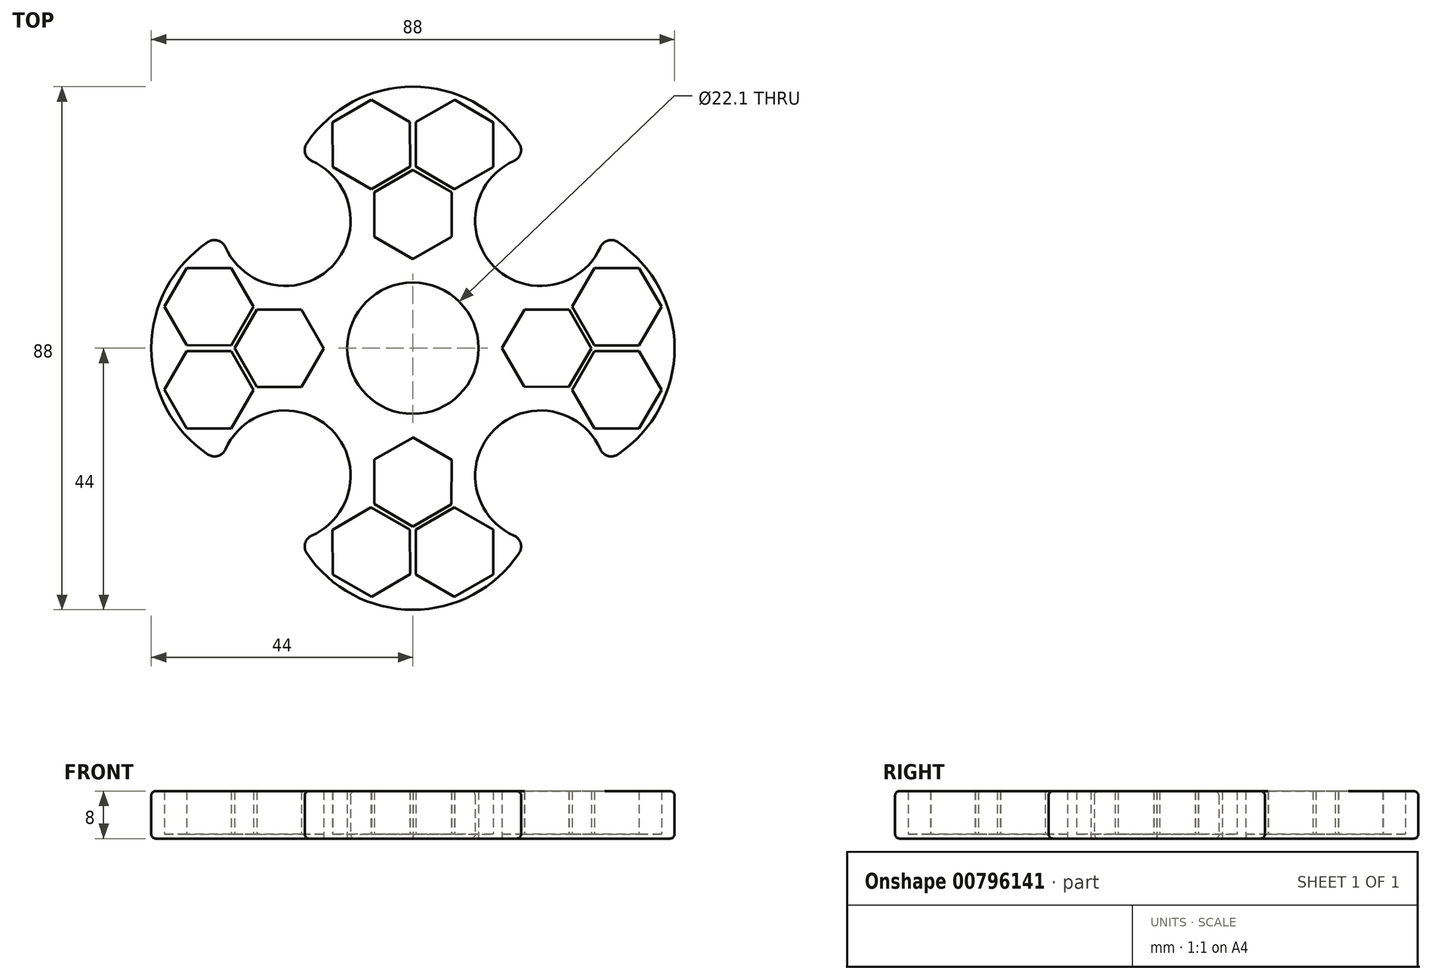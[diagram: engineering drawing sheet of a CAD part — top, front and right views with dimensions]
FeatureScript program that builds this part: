
annotation { "Feature Type Name" : "Feature", "Feature Type Description" : "" }
export const myFeature = defineFeature(function(context is Context, id is Id, definition is map)
    precondition{}
    {
        {
            var Q0;
            Q0=qCreatedBy(makeId("Top.planeOp"),FACE);
            var sketch = newSketch(context, id + "F0", { "sketchPlane" : qUnion([Q0])});
            skCircle(sketch, "E0", {"center": v(0, 0) * mm, "radius": 11.05 * mm});
            skCircle(sketch, "E1", {"center": v(0, 0) * mm, "radius": 35 * mm, "construction": true});
            skPoint(sketch, "E2", {"position": v(-35, 0) * mm});
            skPoint(sketch, "E3", {"position": v(35, 0) * mm});
            skPoint(sketch, "E4", {"position": v(0, 35) * mm});
            skPoint(sketch, "E5", {"position": v(0, -35) * mm});
            skPoint(sketch, "E6.0.midPoint", {"position": v(-28.5, 0) * mm});
            skPoint(sketch, "E7.0.midPoint", {"position": v(28.5, 0) * mm});
            skPoint(sketch, "E8.0.midPoint", {"position": v(0, 28.98) * mm});
            skPoint(sketch, "E9.0.midPoint", {"position": v(0, -28.02) * mm});
            skCircle(sketch, "E10", {"center": v(0, 0) * mm, "radius": 15 * mm});
            skLineSegment(sketch, "E11", {"start": v(0, 0) * mm, "end": v(-35, 0) * mm, "construction": true});
            skLineSegment(sketch, "E12", {"start": v(0, 0) * mm, "end": v(35, 0) * mm, "construction": true});
            skLineSegment(sketch, "E13", {"start": v(0, 0) * mm, "end": v(0, -35) * mm, "construction": true});
            skLineSegment(sketch, "E14", {"start": v(0, 0) * mm, "end": v(0, 35) * mm, "construction": true});
            skLineSegment(sketch, "E15.0", {"start": v(0, 5) * mm, "end": v(-30.51, 5) * mm});
            skLineSegment(sketch, "E16.0", {"start": v(0, -5) * mm, "end": v(30.51, -5) * mm});
            skLineSegment(sketch, "E17.0", {"start": v(0, 5) * mm, "end": v(30.51, 5) * mm});
            skLineSegment(sketch, "E18.0", {"start": v(0, -5) * mm, "end": v(-30.51, -5) * mm});
            skLineSegment(sketch, "E19.0", {"start": v(-5, 0.48) * mm, "end": v(-5, -30.03) * mm});
            skLineSegment(sketch, "E20.0", {"start": v(5, 0.48) * mm, "end": v(5, -30.03) * mm});
            skLineSegment(sketch, "E21.0", {"start": v(5, 0.48) * mm, "end": v(5, 30.98) * mm});
            skLineSegment(sketch, "E22.0", {"start": v(-5, 0.48) * mm, "end": v(-5, 30.98) * mm});
            skLineSegment(sketch, "E23", {"start": v(0, 0) * mm, "end": v(-24.75, 24.75) * mm, "construction": true});
            skLineSegment(sketch, "E24", {"start": v(24.75, -24.75) * mm, "end": v(0, 0) * mm, "construction": true});
            skLineSegment(sketch, "E25", {"start": v(24.75, 24.75) * mm, "end": v(0, 0) * mm, "construction": true});
            skLineSegment(sketch, "E26", {"start": v(-24.75, -24.75) * mm, "end": v(0, 0) * mm, "construction": true});
            skPoint(sketch, "E27", {"position": v(-7, 34.3) * mm});
            skPoint(sketch, "E28", {"position": v(7, 34.3) * mm});
            skPoint(sketch, "E29", {"position": v(-34.3, 7) * mm});
            skPoint(sketch, "E30", {"position": v(-34.3, -7) * mm});
            skPoint(sketch, "E31", {"position": v(34.3, 7) * mm});
            skPoint(sketch, "E32", {"position": v(34.3, -7) * mm});
            skPoint(sketch, "E33", {"position": v(7, -34.3) * mm});
            skPoint(sketch, "E34", {"position": v(-7, -34.3) * mm});
            skCircle(sketch, "E35.cCircle", {"center": v(-7, -34.3) * mm, "radius": 6.5 * mm, "construction": true});
            skLineSegment(sketch, "E35.0", {"start": v(-0.52, -30.5) * mm, "end": v(-0.48, -38.01) * mm});
            skLineSegment(sketch, "E35.1", {"start": v(-0.48, -38.01) * mm, "end": v(-6.96, -41.8) * mm});
            skLineSegment(sketch, "E35.2", {"start": v(-6.96, -41.8) * mm, "end": v(-13.48, -38.08) * mm});
            skLineSegment(sketch, "E35.3", {"start": v(-13.48, -38.08) * mm, "end": v(-13.52, -30.57) * mm});
            skLineSegment(sketch, "E35.4", {"start": v(-13.52, -30.57) * mm, "end": v(-7.04, -26.79) * mm});
            skLineSegment(sketch, "E35.5", {"start": v(-7.04, -26.79) * mm, "end": v(-0.52, -30.5) * mm});
            skPoint(sketch, "E35.0.midPoint", {"position": v(-0.5, -34.26) * mm});
            skPoint(sketch, "E36.0.midPoint", {"position": v(0.5, -30.6) * mm});
            skCircle(sketch, "E37.cCircle", {"center": v(34.3, -7) * mm, "radius": 6.5 * mm, "construction": true});
            skLineSegment(sketch, "E37.0", {"start": v(30.54, -0.5) * mm, "end": v(38.05, -0.5) * mm});
            skLineSegment(sketch, "E37.1", {"start": v(38.05, -0.5) * mm, "end": v(41.8, -7) * mm});
            skLineSegment(sketch, "E37.2", {"start": v(41.8, -7) * mm, "end": v(38.05, -13.5) * mm});
            skLineSegment(sketch, "E37.3", {"start": v(38.05, -13.5) * mm, "end": v(30.54, -13.5) * mm});
            skLineSegment(sketch, "E37.4", {"start": v(30.54, -13.5) * mm, "end": v(26.79, -7) * mm});
            skLineSegment(sketch, "E37.5", {"start": v(26.79, -7) * mm, "end": v(30.54, -0.5) * mm});
            skPoint(sketch, "E37.0.midPoint", {"position": v(34.3, -0.5) * mm});
            skCircle(sketch, "E38.cCircle", {"center": v(34.3, 7) * mm, "radius": 6.5 * mm, "construction": true});
            skLineSegment(sketch, "E38.0", {"start": v(38.05, 0.5) * mm, "end": v(30.54, 0.5) * mm});
            skLineSegment(sketch, "E38.1", {"start": v(30.54, 0.5) * mm, "end": v(26.79, 7) * mm});
            skLineSegment(sketch, "E38.2", {"start": v(26.79, 7) * mm, "end": v(30.54, 13.5) * mm});
            skLineSegment(sketch, "E38.3", {"start": v(30.54, 13.5) * mm, "end": v(38.04, 13.5) * mm});
            skLineSegment(sketch, "E38.4", {"start": v(38.04, 13.5) * mm, "end": v(41.8, 7) * mm});
            skLineSegment(sketch, "E38.5", {"start": v(41.8, 7) * mm, "end": v(38.05, 0.5) * mm});
            skPoint(sketch, "E38.0.midPoint", {"position": v(34.3, 0.5) * mm});
            skCircle(sketch, "E39.cCircle", {"center": v(7, 34.3) * mm, "radius": 6.5 * mm, "construction": true});
            skLineSegment(sketch, "E39.0", {"start": v(0.49, 30.56) * mm, "end": v(0.51, 38.06) * mm});
            skLineSegment(sketch, "E39.1", {"start": v(0.51, 38.06) * mm, "end": v(7.02, 41.8) * mm});
            skLineSegment(sketch, "E39.2", {"start": v(7.02, 41.8) * mm, "end": v(13.51, 38.03) * mm});
            skLineSegment(sketch, "E39.3", {"start": v(13.51, 38.03) * mm, "end": v(13.49, 30.52) * mm});
            skLineSegment(sketch, "E39.4", {"start": v(13.49, 30.52) * mm, "end": v(6.98, 26.79) * mm});
            skLineSegment(sketch, "E39.5", {"start": v(6.98, 26.79) * mm, "end": v(0.49, 30.56) * mm});
            skPoint(sketch, "E39.0.midPoint", {"position": v(0.5, 34.31) * mm});
            skCircle(sketch, "E40.cCircle", {"center": v(-7, 34.3) * mm, "radius": 6.5 * mm, "construction": true});
            skLineSegment(sketch, "E40.0", {"start": v(-0.51, 38.07) * mm, "end": v(-0.49, 30.56) * mm});
            skLineSegment(sketch, "E40.1", {"start": v(-0.49, 30.56) * mm, "end": v(-6.97, 26.79) * mm});
            skLineSegment(sketch, "E40.2", {"start": v(-6.97, 26.79) * mm, "end": v(-13.49, 30.52) * mm});
            skLineSegment(sketch, "E40.3", {"start": v(-13.49, 30.52) * mm, "end": v(-13.51, 38.02) * mm});
            skLineSegment(sketch, "E40.4", {"start": v(-13.51, 38.02) * mm, "end": v(-7.03, 41.8) * mm});
            skLineSegment(sketch, "E40.5", {"start": v(-7.03, 41.8) * mm, "end": v(-0.51, 38.07) * mm});
            skPoint(sketch, "E40.0.midPoint", {"position": v(-0.5, 34.32) * mm});
            skCircle(sketch, "E41.cCircle", {"center": v(-34.3, 7) * mm, "radius": 6.5 * mm, "construction": true});
            skLineSegment(sketch, "E41.0", {"start": v(-30.55, 0.5) * mm, "end": v(-38.05, 0.5) * mm});
            skLineSegment(sketch, "E41.1", {"start": v(-38.05, 0.5) * mm, "end": v(-41.8, 7) * mm});
            skLineSegment(sketch, "E41.2", {"start": v(-41.8, 7) * mm, "end": v(-38.04, 13.5) * mm});
            skLineSegment(sketch, "E41.3", {"start": v(-38.04, 13.5) * mm, "end": v(-30.53, 13.5) * mm});
            skLineSegment(sketch, "E41.4", {"start": v(-30.53, 13.5) * mm, "end": v(-26.79, 7) * mm});
            skLineSegment(sketch, "E41.5", {"start": v(-26.79, 7) * mm, "end": v(-30.55, 0.5) * mm});
            skPoint(sketch, "E41.0.midPoint", {"position": v(-34.3, 0.5) * mm});
            skCircle(sketch, "E42.cCircle", {"center": v(-34.3, -7) * mm, "radius": 6.5 * mm, "construction": true});
            skLineSegment(sketch, "E42.0", {"start": v(-38.03, -0.5) * mm, "end": v(-30.53, -0.5) * mm});
            skLineSegment(sketch, "E42.1", {"start": v(-30.53, -0.5) * mm, "end": v(-26.79, -7.01) * mm});
            skLineSegment(sketch, "E42.2", {"start": v(-26.79, -7.01) * mm, "end": v(-30.55, -13.5) * mm});
            skLineSegment(sketch, "E42.3", {"start": v(-30.55, -13.5) * mm, "end": v(-38.06, -13.5) * mm});
            skLineSegment(sketch, "E42.4", {"start": v(-38.06, -13.5) * mm, "end": v(-41.8, -6.99) * mm});
            skLineSegment(sketch, "E42.5", {"start": v(-41.8, -6.99) * mm, "end": v(-38.03, -0.5) * mm});
            skPoint(sketch, "E42.0.midPoint", {"position": v(-34.28, -0.5) * mm});
            skCircle(sketch, "E43", {"center": v(0, 0) * mm, "radius": 22.5 * mm, "construction": true});
            skPoint(sketch, "E44", {"position": v(-22.5, 0) * mm});
            skPoint(sketch, "E45", {"position": v(0, 22.5) * mm});
            skPoint(sketch, "E46", {"position": v(22.5, 0) * mm});
            skPoint(sketch, "E47", {"position": v(0, -22.5) * mm});
            skCircle(sketch, "E48.cCircle", {"center": v(7, -34.3) * mm, "radius": 6.5 * mm, "construction": true});
            skLineSegment(sketch, "E48.0", {"start": v(0.5, -38.05) * mm, "end": v(0.5, -30.54) * mm});
            skLineSegment(sketch, "E48.1", {"start": v(0.5, -30.54) * mm, "end": v(7, -26.79) * mm});
            skLineSegment(sketch, "E48.2", {"start": v(7, -26.79) * mm, "end": v(13.5, -30.54) * mm});
            skLineSegment(sketch, "E48.3", {"start": v(13.5, -30.54) * mm, "end": v(13.5, -38.05) * mm});
            skLineSegment(sketch, "E48.4", {"start": v(13.5, -38.05) * mm, "end": v(7, -41.8) * mm});
            skLineSegment(sketch, "E48.5", {"start": v(7, -41.8) * mm, "end": v(0.5, -38.05) * mm});
            skPoint(sketch, "E48.0.midPoint", {"position": v(0.5, -34.3) * mm});
            skCircle(sketch, "E49.cCircle", {"center": v(0, 22.5) * mm, "radius": 6.5 * mm, "construction": true});
            skLineSegment(sketch, "E49.0", {"start": v(0, 15) * mm, "end": v(-6.5, 18.74) * mm});
            skLineSegment(sketch, "E49.1", {"start": v(-6.5, 18.74) * mm, "end": v(-6.5, 26.25) * mm});
            skLineSegment(sketch, "E49.2", {"start": v(-6.5, 26.25) * mm, "end": v(0, 30) * mm});
            skLineSegment(sketch, "E49.3", {"start": v(0, 30) * mm, "end": v(6.5, 26.26) * mm});
            skLineSegment(sketch, "E49.4", {"start": v(6.5, 26.26) * mm, "end": v(6.5, 18.75) * mm});
            skLineSegment(sketch, "E49.5", {"start": v(6.5, 18.75) * mm, "end": v(0, 15) * mm});
            skPoint(sketch, "E49.0.midPoint", {"position": v(-3.24, 16.87) * mm});
            skCircle(sketch, "E50.cCircle", {"center": v(-22.5, 0) * mm, "radius": 6.5 * mm, "construction": true});
            skLineSegment(sketch, "E50.0", {"start": v(-15, -0.02) * mm, "end": v(-18.76, -6.5) * mm});
            skLineSegment(sketch, "E50.1", {"start": v(-18.76, -6.5) * mm, "end": v(-26.27, -6.5) * mm});
            skLineSegment(sketch, "E50.2", {"start": v(-26.27, -6.5) * mm, "end": v(-30, 0.02) * mm});
            skLineSegment(sketch, "E50.3", {"start": v(-30, 0.02) * mm, "end": v(-26.24, 6.5) * mm});
            skLineSegment(sketch, "E50.4", {"start": v(-26.24, 6.5) * mm, "end": v(-18.73, 6.5) * mm});
            skLineSegment(sketch, "E50.5", {"start": v(-18.73, 6.5) * mm, "end": v(-15, -0.02) * mm});
            skPoint(sketch, "E50.0.midPoint", {"position": v(-16.88, -3.26) * mm});
            skCircle(sketch, "E51.cCircle", {"center": v(0, -22.5) * mm, "radius": 6.5 * mm, "construction": true});
            skLineSegment(sketch, "E51.0", {"start": v(-0.03, -30) * mm, "end": v(-6.51, -26.23) * mm});
            skLineSegment(sketch, "E51.1", {"start": v(-6.51, -26.23) * mm, "end": v(-6.49, -18.72) * mm});
            skLineSegment(sketch, "E51.2", {"start": v(-6.49, -18.72) * mm, "end": v(0.03, -15) * mm});
            skLineSegment(sketch, "E51.3", {"start": v(0.03, -15) * mm, "end": v(6.51, -18.77) * mm});
            skLineSegment(sketch, "E51.4", {"start": v(6.51, -18.77) * mm, "end": v(6.49, -26.28) * mm});
            skLineSegment(sketch, "E51.5", {"start": v(6.49, -26.28) * mm, "end": v(-0.03, -30) * mm});
            skPoint(sketch, "E51.0.midPoint", {"position": v(-3.27, -28.12) * mm});
            skCircle(sketch, "E52.cCircle", {"center": v(22.5, 0) * mm, "radius": 6.5 * mm, "construction": true});
            skLineSegment(sketch, "E52.0", {"start": v(30, -0.04) * mm, "end": v(26.22, -6.52) * mm});
            skLineSegment(sketch, "E52.1", {"start": v(26.22, -6.52) * mm, "end": v(18.71, -6.48) * mm});
            skLineSegment(sketch, "E52.2", {"start": v(18.71, -6.48) * mm, "end": v(15, 0.04) * mm});
            skLineSegment(sketch, "E52.3", {"start": v(15, 0.04) * mm, "end": v(18.78, 6.52) * mm});
            skLineSegment(sketch, "E52.4", {"start": v(18.78, 6.52) * mm, "end": v(26.29, 6.48) * mm});
            skLineSegment(sketch, "E52.5", {"start": v(26.29, 6.48) * mm, "end": v(30, -0.04) * mm});
            skPoint(sketch, "E52.0.midPoint", {"position": v(28.11, -3.28) * mm});
            skCircle(sketch, "E53", {"center": v(22.5, 0) * mm, "radius": 21.5 * mm});
            skCircle(sketch, "E54", {"center": v(0, 22.5) * mm, "radius": 21.5 * mm});
            skCircle(sketch, "E55", {"center": v(-22.5, 0) * mm, "radius": 21.5 * mm});
            skCircle(sketch, "E56", {"center": v(0, -22.5) * mm, "radius": 21.5 * mm});
            skPoint(sketch, "E57", {"position": v(-21.48, -21.48) * mm});
            skPoint(sketch, "E58", {"position": v(21.48, -21.48) * mm});
            skPoint(sketch, "E59", {"position": v(21.48, 21.48) * mm});
            skPoint(sketch, "E60", {"position": v(-21.48, 21.48) * mm});
            skCircle(sketch, "E61", {"center": v(-21.48, -21.48) * mm, "radius": 11 * mm});
            skCircle(sketch, "E62", {"center": v(-21.48, 21.48) * mm, "radius": 11 * mm});
            skCircle(sketch, "E63", {"center": v(21.48, 21.48) * mm, "radius": 11 * mm});
            skCircle(sketch, "E64", {"center": v(21.48, -21.48) * mm, "radius": 11 * mm});
            skSolve(sketch);
        }
        {
            var Q0;
            {var subQ18=sQuery(id+"F0.wireOp",EDGE,"E41.0");Q0=makeQuery(id+"F0.imprint","IMPRINT",FACE,{"disambiguationData":[TD([[makeQuery(id+"F0.imprint","IMPRINT",EDGE,{"derivedFrom":subQ18}),1.0]])]});}
            var Q1;
            {var subQ23=sQuery(id+"F0.wireOp",EDGE,"E39.0");Q1=makeQuery(id+"F0.imprint","IMPRINT",FACE,{"disambiguationData":[TD([[makeQuery(id+"F0.imprint","IMPRINT",EDGE,{"derivedFrom":subQ23}),1.0]])]});}
            var Q2;
            {var subQ18=sQuery(id+"F0.wireOp",EDGE,"E37.0");Q2=makeQuery(id+"F0.imprint","IMPRINT",FACE,{"disambiguationData":[TD([[makeQuery(id+"F0.imprint","IMPRINT",EDGE,{"derivedFrom":subQ18}),1.0]])]});}
            var Q3;
            {var subQ18=sQuery(id+"F0.wireOp",EDGE,"E35.0");Q3=makeQuery(id+"F0.imprint","IMPRINT",FACE,{"disambiguationData":[TD([[makeQuery(id+"F0.imprint","IMPRINT",EDGE,{"derivedFrom":subQ18}),1.0]])]});}
            var Q4;
            {var subQ1=sQuery(id+"F0.wireOp",EDGE,"E0");var subQ8=sQuery(id+"F0.wireOp",EDGE,"E18.0");var subQ10=makeQuery(id+"F0.imprint","INTERSECT",VERTEX,{"derivedFrom":[subQ1,subQ8]});Q4=makeQuery(id+"F0.imprint","IMPRINT",FACE,{"disambiguationData":[TD([[makeQuery(id+"F0.imprint","IMPRINT",EDGE,{"disambiguationData":[TD([[subQ10,-1.0]])],"derivedFrom":subQ1}),-1.0]])]});}
            var Q5;
            {var subQ3=sQuery(id+"F0.wireOp",EDGE,"E54");var subQ9=sQuery(id+"F0.wireOp",EDGE,"E0");var subQ10=makeQuery(id+"F0.imprint","INTERSECT",VERTEX,{"disambiguationData":[OD(1.0)],"derivedFrom":[subQ9,subQ3]});Q5=makeQuery(id+"F0.imprint","IMPRINT",FACE,{"disambiguationData":[TD([[makeQuery(id+"F0.imprint","IMPRINT",EDGE,{"disambiguationData":[TD([[subQ10,-1.0]])],"derivedFrom":subQ9}),-1.0]])]});}
            var Q6;
            {var subQ0=sQuery(id+"F0.wireOp",EDGE,"E22.0");var subQ1=sQuery(id+"F0.wireOp",EDGE,"E0");var subQ2=makeQuery(id+"F0.imprint","INTERSECT",VERTEX,{"derivedFrom":[subQ1,subQ0]});Q6=makeQuery(id+"F0.imprint","IMPRINT",FACE,{"disambiguationData":[TD([[makeQuery(id+"F0.imprint","IMPRINT",EDGE,{"disambiguationData":[TD([[subQ2,-1.0]])],"derivedFrom":subQ1}),-1.0]])]});}
            var Q7;
            {var subQ3=sQuery(id+"F0.wireOp",EDGE,"E53");var subQ11=sQuery(id+"F0.wireOp",EDGE,"E0");var subQ16=makeQuery(id+"F0.imprint","INTERSECT",VERTEX,{"disambiguationData":[OD(0.0)],"derivedFrom":[subQ11,subQ3]});Q7=makeQuery(id+"F0.imprint","IMPRINT",FACE,{"disambiguationData":[TD([[makeQuery(id+"F0.imprint","IMPRINT",EDGE,{"disambiguationData":[TD([[subQ16,-1.0]])],"derivedFrom":subQ11}),-1.0]])]});}
            var Q8;
            {var subQ0=sQuery(id+"F0.wireOp",EDGE,"E17.0");var subQ1=sQuery(id+"F0.wireOp",EDGE,"E0");var subQ2=makeQuery(id+"F0.imprint","INTERSECT",VERTEX,{"derivedFrom":[subQ1,subQ0]});Q8=makeQuery(id+"F0.imprint","IMPRINT",FACE,{"disambiguationData":[TD([[makeQuery(id+"F0.imprint","IMPRINT",EDGE,{"disambiguationData":[TD([[subQ2,-1.0]])],"derivedFrom":subQ1}),-1.0]])]});}
            var Q9;
            {var subQ5=sQuery(id+"F0.wireOp",EDGE,"E0");var subQ13=sQuery(id+"F0.wireOp",EDGE,"E54");var subQ14=makeQuery(id+"F0.imprint","INTERSECT",VERTEX,{"disambiguationData":[OD(0.0)],"derivedFrom":[subQ5,subQ13]});Q9=makeQuery(id+"F0.imprint","IMPRINT",FACE,{"disambiguationData":[TD([[makeQuery(id+"F0.imprint","IMPRINT",EDGE,{"disambiguationData":[TD([[subQ14,1.0]])],"derivedFrom":subQ5}),-1.0]])]});}
            var Q10;
            {var subQ0=sQuery(id+"F0.wireOp",EDGE,"E20.0");var subQ1=sQuery(id+"F0.wireOp",EDGE,"E0");var subQ2=makeQuery(id+"F0.imprint","INTERSECT",VERTEX,{"derivedFrom":[subQ1,subQ0]});Q10=makeQuery(id+"F0.imprint","IMPRINT",FACE,{"disambiguationData":[TD([[makeQuery(id+"F0.imprint","IMPRINT",EDGE,{"disambiguationData":[TD([[subQ2,-1.0]])],"derivedFrom":subQ1}),-1.0]])]});}
            var Q11;
            {var subQ7=sQuery(id+"F0.wireOp",EDGE,"E55");var subQ12=sQuery(id+"F0.wireOp",EDGE,"E0");var subQ13=makeQuery(id+"F0.imprint","INTERSECT",VERTEX,{"disambiguationData":[OD(1.0)],"derivedFrom":[subQ12,subQ7]});Q11=makeQuery(id+"F0.imprint","IMPRINT",FACE,{"disambiguationData":[TD([[makeQuery(id+"F0.imprint","IMPRINT",EDGE,{"disambiguationData":[TD([[subQ13,-1.0]])],"derivedFrom":subQ12}),-1.0]])]});}
            var Q12;
            {var subQ0=sQuery(id+"F0.wireOp",EDGE,"E56");var subQ1=sQuery(id+"F0.wireOp",EDGE,"E10");var subQ2=makeQuery(id+"F0.imprint","INTERSECT",VERTEX,{"disambiguationData":[OD(0.0)],"derivedFrom":[subQ1,subQ0]});Q12=makeQuery(id+"F0.imprint","IMPRINT",FACE,{"disambiguationData":[TD([[makeQuery(id+"F0.imprint","IMPRINT",EDGE,{"disambiguationData":[TD([[subQ2,-1.0]])],"derivedFrom":subQ1}),-1.0]])]});}
            var Q13;
            {var subQ0=sQuery(id+"F0.wireOp",EDGE,"E55");var subQ1=sQuery(id+"F0.wireOp",EDGE,"E10");var subQ2=makeQuery(id+"F0.imprint","INTERSECT",VERTEX,{"disambiguationData":[OD(0.0)],"derivedFrom":[subQ1,subQ0]});Q13=makeQuery(id+"F0.imprint","IMPRINT",FACE,{"disambiguationData":[TD([[makeQuery(id+"F0.imprint","IMPRINT",EDGE,{"disambiguationData":[TD([[subQ2,-1.0]])],"derivedFrom":subQ1}),-1.0]])]});}
            var Q14;
            {var subQ0=sQuery(id+"F0.wireOp",EDGE,"E54");var subQ1=sQuery(id+"F0.wireOp",EDGE,"E10");var subQ2=makeQuery(id+"F0.imprint","INTERSECT",VERTEX,{"disambiguationData":[OD(0.0)],"derivedFrom":[subQ1,subQ0]});Q14=makeQuery(id+"F0.imprint","IMPRINT",FACE,{"disambiguationData":[TD([[makeQuery(id+"F0.imprint","IMPRINT",EDGE,{"disambiguationData":[TD([[subQ2,-1.0]])],"derivedFrom":subQ1}),-1.0]])]});}
            var Q15;
            {var subQ0=sQuery(id+"F0.wireOp",EDGE,"E53");var subQ1=sQuery(id+"F0.wireOp",EDGE,"E10");var subQ2=makeQuery(id+"F0.imprint","INTERSECT",VERTEX,{"disambiguationData":[OD(1.0)],"derivedFrom":[subQ1,subQ0]});Q15=makeQuery(id+"F0.imprint","IMPRINT",FACE,{"disambiguationData":[TD([[makeQuery(id+"F0.imprint","IMPRINT",EDGE,{"disambiguationData":[TD([[subQ2,-1.0]])],"derivedFrom":subQ1}),-1.0]])]});}
            var Q16;
            {var subQ0=sQuery(id+"F0.wireOp",EDGE,"E50.0");var subQ1=sQuery(id+"F0.wireOp",EDGE,"E10");var subQ2=makeQuery(id+"F0.imprint","INTERSECT",VERTEX,{"derivedFrom":[subQ1,subQ0]});Q16=makeQuery(id+"F0.imprint","IMPRINT",FACE,{"disambiguationData":[TD([[makeQuery(id+"F0.imprint","IMPRINT",EDGE,{"disambiguationData":[TD([[subQ2,-1.0]])],"derivedFrom":subQ1}),-1.0]])]});}
            var Q17;
            {var subQ0=sQuery(id+"F0.wireOp",EDGE,"E15.0");var subQ1=sQuery(id+"F0.wireOp",EDGE,"E10");var subQ2=makeQuery(id+"F0.imprint","INTERSECT",VERTEX,{"derivedFrom":[subQ1,subQ0]});Q17=makeQuery(id+"F0.imprint","IMPRINT",FACE,{"disambiguationData":[TD([[makeQuery(id+"F0.imprint","IMPRINT",EDGE,{"disambiguationData":[TD([[subQ2,-1.0]])],"derivedFrom":subQ1}),-1.0]])]});}
            var Q18;
            {var subQ0=sQuery(id+"F0.wireOp",EDGE,"E49.0");var subQ1=sQuery(id+"F0.wireOp",EDGE,"E10");var subQ2=makeQuery(id+"F0.imprint","INTERSECT",VERTEX,{"derivedFrom":[subQ1,subQ0]});Q18=makeQuery(id+"F0.imprint","IMPRINT",FACE,{"disambiguationData":[TD([[makeQuery(id+"F0.imprint","IMPRINT",EDGE,{"disambiguationData":[TD([[subQ2,-1.0]])],"derivedFrom":subQ1}),-1.0]])]});}
            var Q19;
            {var subQ0=sQuery(id+"F0.wireOp",EDGE,"E21.0");var subQ1=sQuery(id+"F0.wireOp",EDGE,"E10");var subQ2=makeQuery(id+"F0.imprint","INTERSECT",VERTEX,{"derivedFrom":[subQ1,subQ0]});Q19=makeQuery(id+"F0.imprint","IMPRINT",FACE,{"disambiguationData":[TD([[makeQuery(id+"F0.imprint","IMPRINT",EDGE,{"disambiguationData":[TD([[subQ2,-1.0]])],"derivedFrom":subQ1}),-1.0]])]});}
            var Q20;
            {var subQ0=sQuery(id+"F0.wireOp",EDGE,"E52.3");var subQ1=sQuery(id+"F0.wireOp",EDGE,"E10");var subQ2=makeQuery(id+"F0.imprint","INTERSECT",VERTEX,{"derivedFrom":[subQ1,subQ0]});Q20=makeQuery(id+"F0.imprint","IMPRINT",FACE,{"disambiguationData":[TD([[makeQuery(id+"F0.imprint","IMPRINT",EDGE,{"disambiguationData":[TD([[subQ2,-1.0]])],"derivedFrom":subQ1}),-1.0]])]});}
            var Q21;
            {var subQ0=sQuery(id+"F0.wireOp",EDGE,"E52.2");var subQ1=sQuery(id+"F0.wireOp",EDGE,"E10");var subQ2=makeQuery(id+"F0.imprint","INTERSECT",VERTEX,{"derivedFrom":[subQ1,subQ0]});Q21=makeQuery(id+"F0.imprint","IMPRINT",FACE,{"disambiguationData":[TD([[makeQuery(id+"F0.imprint","IMPRINT",EDGE,{"disambiguationData":[TD([[subQ2,1.0]])],"derivedFrom":subQ1}),-1.0]])]});}
            var Q22;
            {var subQ0=sQuery(id+"F0.wireOp",EDGE,"E51.3");var subQ1=sQuery(id+"F0.wireOp",EDGE,"E10");var subQ2=makeQuery(id+"F0.imprint","INTERSECT",VERTEX,{"derivedFrom":[subQ1,subQ0]});Q22=makeQuery(id+"F0.imprint","IMPRINT",FACE,{"disambiguationData":[TD([[makeQuery(id+"F0.imprint","IMPRINT",EDGE,{"disambiguationData":[TD([[subQ2,-1.0]])],"derivedFrom":subQ1}),-1.0]])]});}
            var Q23;
            {var subQ0=sQuery(id+"F0.wireOp",EDGE,"E19.0");var subQ1=sQuery(id+"F0.wireOp",EDGE,"E10");var subQ2=makeQuery(id+"F0.imprint","INTERSECT",VERTEX,{"derivedFrom":[subQ1,subQ0]});Q23=makeQuery(id+"F0.imprint","IMPRINT",FACE,{"disambiguationData":[TD([[makeQuery(id+"F0.imprint","IMPRINT",EDGE,{"disambiguationData":[TD([[subQ2,-1.0]])],"derivedFrom":subQ1}),-1.0]])]});}
            var Q24;
            {var subQ0=sQuery(id+"F0.wireOp",EDGE,"E22.0");var subQ1=sQuery(id+"F0.wireOp",EDGE,"E10");var subQ2=makeQuery(id+"F0.imprint","INTERSECT",VERTEX,{"derivedFrom":[subQ1,subQ0]});Q24=makeQuery(id+"F0.imprint","IMPRINT",FACE,{"disambiguationData":[TD([[makeQuery(id+"F0.imprint","IMPRINT",EDGE,{"disambiguationData":[TD([[subQ2,-1.0]])],"derivedFrom":subQ1}),1.0]])]});}
            var Q25;
            {var subQ0=sQuery(id+"F0.wireOp",EDGE,"E55");var subQ1=sQuery(id+"F0.wireOp",EDGE,"E0");var subQ2=makeQuery(id+"F0.imprint","INTERSECT",VERTEX,{"disambiguationData":[OD(0.0)],"derivedFrom":[subQ1,subQ0]});Q25=makeQuery(id+"F0.imprint","IMPRINT",FACE,{"disambiguationData":[TD([[makeQuery(id+"F0.imprint","IMPRINT",EDGE,{"disambiguationData":[TD([[subQ2,-1.0]])],"derivedFrom":subQ1}),-1.0]])]});}
            var Q26;
            {var subQ0=sQuery(id+"F0.wireOp",EDGE,"E21.0");var subQ1=sQuery(id+"F0.wireOp",EDGE,"E0");var subQ2=makeQuery(id+"F0.imprint","INTERSECT",VERTEX,{"derivedFrom":[subQ1,subQ0]});Q26=makeQuery(id+"F0.imprint","IMPRINT",FACE,{"disambiguationData":[TD([[makeQuery(id+"F0.imprint","IMPRINT",EDGE,{"disambiguationData":[TD([[subQ2,-1.0]])],"derivedFrom":subQ1}),-1.0]])]});}
            var Q27;
            {var subQ0=sQuery(id+"F0.wireOp",EDGE,"E17.0");var subQ1=sQuery(id+"F0.wireOp",EDGE,"E10");var subQ2=makeQuery(id+"F0.imprint","INTERSECT",VERTEX,{"derivedFrom":[subQ1,subQ0]});Q27=makeQuery(id+"F0.imprint","IMPRINT",FACE,{"disambiguationData":[TD([[makeQuery(id+"F0.imprint","IMPRINT",EDGE,{"disambiguationData":[TD([[subQ2,-1.0]])],"derivedFrom":subQ1}),1.0]])]});}
            var Q28;
            {var subQ0=sQuery(id+"F0.wireOp",EDGE,"E53");var subQ1=sQuery(id+"F0.wireOp",EDGE,"E10");var subQ2=makeQuery(id+"F0.imprint","INTERSECT",VERTEX,{"disambiguationData":[OD(0.0)],"derivedFrom":[subQ1,subQ0]});Q28=makeQuery(id+"F0.imprint","IMPRINT",FACE,{"disambiguationData":[TD([[makeQuery(id+"F0.imprint","IMPRINT",EDGE,{"disambiguationData":[TD([[subQ2,-1.0]])],"derivedFrom":subQ1}),1.0]])]});}
            var Q29;
            {var subQ0=sQuery(id+"F0.wireOp",EDGE,"E17.0");var subQ1=sQuery(id+"F0.wireOp",EDGE,"E0");var subQ2=makeQuery(id+"F0.imprint","INTERSECT",VERTEX,{"derivedFrom":[subQ1,subQ0]});Q29=makeQuery(id+"F0.imprint","IMPRINT",FACE,{"disambiguationData":[TD([[makeQuery(id+"F0.imprint","IMPRINT",EDGE,{"disambiguationData":[TD([[subQ2,1.0]])],"derivedFrom":subQ1}),-1.0]])]});}
            var Q30;
            {var subQ0=sQuery(id+"F0.wireOp",EDGE,"E56");var subQ1=sQuery(id+"F0.wireOp",EDGE,"E10");var subQ2=makeQuery(id+"F0.imprint","INTERSECT",VERTEX,{"disambiguationData":[OD(1.0)],"derivedFrom":[subQ1,subQ0]});Q30=makeQuery(id+"F0.imprint","IMPRINT",FACE,{"disambiguationData":[TD([[makeQuery(id+"F0.imprint","IMPRINT",EDGE,{"disambiguationData":[TD([[subQ2,-1.0]])],"derivedFrom":subQ1}),1.0]])]});}
            var Q31;
            {var subQ0=sQuery(id+"F0.wireOp",EDGE,"E16.0");var subQ1=sQuery(id+"F0.wireOp",EDGE,"E0");var subQ2=makeQuery(id+"F0.imprint","INTERSECT",VERTEX,{"derivedFrom":[subQ1,subQ0]});Q31=makeQuery(id+"F0.imprint","IMPRINT",FACE,{"disambiguationData":[TD([[makeQuery(id+"F0.imprint","IMPRINT",EDGE,{"disambiguationData":[TD([[subQ2,-1.0]])],"derivedFrom":subQ1}),-1.0]])]});}
            var Q32;
            {var subQ0=sQuery(id+"F0.wireOp",EDGE,"E20.0");var subQ1=sQuery(id+"F0.wireOp",EDGE,"E10");var subQ2=makeQuery(id+"F0.imprint","INTERSECT",VERTEX,{"derivedFrom":[subQ1,subQ0]});Q32=makeQuery(id+"F0.imprint","IMPRINT",FACE,{"disambiguationData":[TD([[makeQuery(id+"F0.imprint","IMPRINT",EDGE,{"disambiguationData":[TD([[subQ2,-1.0]])],"derivedFrom":subQ1}),1.0]])]});}
            var Q33;
            {var subQ0=sQuery(id+"F0.wireOp",EDGE,"E53");var subQ1=sQuery(id+"F0.wireOp",EDGE,"E0");var subQ2=makeQuery(id+"F0.imprint","INTERSECT",VERTEX,{"disambiguationData":[OD(1.0)],"derivedFrom":[subQ1,subQ0]});Q33=makeQuery(id+"F0.imprint","IMPRINT",FACE,{"disambiguationData":[TD([[makeQuery(id+"F0.imprint","IMPRINT",EDGE,{"disambiguationData":[TD([[subQ2,-1.0]])],"derivedFrom":subQ1}),-1.0]])]});}
            var Q34;
            {var subQ0=sQuery(id+"F0.wireOp",EDGE,"E19.0");var subQ1=sQuery(id+"F0.wireOp",EDGE,"E0");var subQ2=makeQuery(id+"F0.imprint","INTERSECT",VERTEX,{"derivedFrom":[subQ1,subQ0]});Q34=makeQuery(id+"F0.imprint","IMPRINT",FACE,{"disambiguationData":[TD([[makeQuery(id+"F0.imprint","IMPRINT",EDGE,{"disambiguationData":[TD([[subQ2,-1.0]])],"derivedFrom":subQ1}),-1.0]])]});}
            var Q35;
            {var subQ0=sQuery(id+"F0.wireOp",EDGE,"E55");var subQ1=sQuery(id+"F0.wireOp",EDGE,"E10");var subQ2=makeQuery(id+"F0.imprint","INTERSECT",VERTEX,{"disambiguationData":[OD(1.0)],"derivedFrom":[subQ1,subQ0]});Q35=makeQuery(id+"F0.imprint","IMPRINT",FACE,{"disambiguationData":[TD([[makeQuery(id+"F0.imprint","IMPRINT",EDGE,{"disambiguationData":[TD([[subQ2,-1.0]])],"derivedFrom":subQ1}),1.0]])]});}
            var Q36;
            {var subQ0=sQuery(id+"F0.wireOp",EDGE,"E56");var subQ1=sQuery(id+"F0.wireOp",EDGE,"E0");var subQ2=makeQuery(id+"F0.imprint","INTERSECT",VERTEX,{"disambiguationData":[OD(0.0)],"derivedFrom":[subQ1,subQ0]});Q36=makeQuery(id+"F0.imprint","IMPRINT",FACE,{"disambiguationData":[TD([[makeQuery(id+"F0.imprint","IMPRINT",EDGE,{"disambiguationData":[TD([[subQ2,-1.0]])],"derivedFrom":subQ1}),-1.0]])]});}
            var Q37;
            {var subQ0=sQuery(id+"F0.wireOp",EDGE,"E18.0");var subQ1=sQuery(id+"F0.wireOp",EDGE,"E10");var subQ2=makeQuery(id+"F0.imprint","INTERSECT",VERTEX,{"derivedFrom":[subQ1,subQ0]});Q37=makeQuery(id+"F0.imprint","IMPRINT",FACE,{"disambiguationData":[TD([[makeQuery(id+"F0.imprint","IMPRINT",EDGE,{"disambiguationData":[TD([[subQ2,-1.0]])],"derivedFrom":subQ1}),1.0]])]});}
            var Q38;
            {var subQ0=sQuery(id+"F0.wireOp",EDGE,"E15.0");var subQ1=sQuery(id+"F0.wireOp",EDGE,"E0");var subQ2=makeQuery(id+"F0.imprint","INTERSECT",VERTEX,{"derivedFrom":[subQ1,subQ0]});Q38=makeQuery(id+"F0.imprint","IMPRINT",FACE,{"disambiguationData":[TD([[makeQuery(id+"F0.imprint","IMPRINT",EDGE,{"disambiguationData":[TD([[subQ2,-1.0]])],"derivedFrom":subQ1}),-1.0]])]});}
            var Q39;
            {var subQ0=sQuery(id+"F0.wireOp",EDGE,"E54");var subQ1=sQuery(id+"F0.wireOp",EDGE,"E10");var subQ2=makeQuery(id+"F0.imprint","INTERSECT",VERTEX,{"disambiguationData":[OD(1.0)],"derivedFrom":[subQ1,subQ0]});Q39=makeQuery(id+"F0.imprint","IMPRINT",FACE,{"disambiguationData":[TD([[makeQuery(id+"F0.imprint","IMPRINT",EDGE,{"disambiguationData":[TD([[subQ2,-1.0]])],"derivedFrom":subQ1}),1.0]])]});}
            extrude(context, id + "F1", {"entities" : qUnion([Q0, Q1, Q2, Q3, Q4, Q5, Q6, Q7, Q8, Q9, Q10, Q11, Q12, Q13, Q14, Q15, Q16, Q17, Q18, Q19, Q20, Q21, Q22, Q23, Q24, Q25, Q26, Q27, Q28, Q29, Q30, Q31, Q32, Q33, Q34, Q35, Q36, Q37, Q38, Q39]), "depth" : 8 * mm, "offsetDistance" : 25 * mm});
        }
        {
            var Q0;
            {var subQ1=sQuery(id+"F0.wireOp",EDGE,"E10");var subQ8=sQuery(id+"F0.wireOp",EDGE,"E50.5");var subQ13=makeQuery(id+"F0.imprint","INTERSECT",VERTEX,{"derivedFrom":[subQ1,subQ8]});Q0=makeQuery(id+"F0.imprint","IMPRINT",FACE,{"disambiguationData":[TD([[makeQuery(id+"F0.imprint","IMPRINT",EDGE,{"disambiguationData":[TD([[subQ13,-1.0]])],"derivedFrom":subQ1}),-1.0]])]});}
            var Q1;
            {var subQ0=sQuery(id+"F0.wireOp",EDGE,"E41.0");Q1=makeQuery(id+"F0.imprint","IMPRINT",FACE,{"disambiguationData":[TD([[makeQuery(id+"F0.imprint","IMPRINT",EDGE,{"derivedFrom":subQ0}),-1.0]])]});}
            var Q2;
            {var subQ3=sQuery(id+"F0.wireOp",EDGE,"E42.0");Q2=makeQuery(id+"F0.imprint","IMPRINT",FACE,{"disambiguationData":[TD([[makeQuery(id+"F0.imprint","IMPRINT",EDGE,{"derivedFrom":subQ3}),-1.0]])]});}
            var Q3;
            {var subQ3=sQuery(id+"F0.wireOp",EDGE,"E40.0");Q3=makeQuery(id+"F0.imprint","IMPRINT",FACE,{"disambiguationData":[TD([[makeQuery(id+"F0.imprint","IMPRINT",EDGE,{"derivedFrom":subQ3}),-1.0]])]});}
            var Q4;
            {var subQ0=sQuery(id+"F0.wireOp",EDGE,"E39.0");Q4=makeQuery(id+"F0.imprint","IMPRINT",FACE,{"disambiguationData":[TD([[makeQuery(id+"F0.imprint","IMPRINT",EDGE,{"derivedFrom":subQ0}),-1.0]])]});}
            var Q5;
            {var subQ5=sQuery(id+"F0.wireOp",EDGE,"E10");var subQ10=sQuery(id+"F0.wireOp",EDGE,"E49.5");var subQ12=makeQuery(id+"F0.imprint","INTERSECT",VERTEX,{"derivedFrom":[subQ5,subQ10]});Q5=makeQuery(id+"F0.imprint","IMPRINT",FACE,{"disambiguationData":[TD([[makeQuery(id+"F0.imprint","IMPRINT",EDGE,{"disambiguationData":[TD([[subQ12,-1.0]])],"derivedFrom":subQ5}),-1.0]])]});}
            var Q6;
            {var subQ3=sQuery(id+"F0.wireOp",EDGE,"E38.0");Q6=makeQuery(id+"F0.imprint","IMPRINT",FACE,{"disambiguationData":[TD([[makeQuery(id+"F0.imprint","IMPRINT",EDGE,{"derivedFrom":subQ3}),-1.0]])]});}
            var Q7;
            {var subQ0=sQuery(id+"F0.wireOp",EDGE,"E37.0");Q7=makeQuery(id+"F0.imprint","IMPRINT",FACE,{"disambiguationData":[TD([[makeQuery(id+"F0.imprint","IMPRINT",EDGE,{"derivedFrom":subQ0}),-1.0]])]});}
            var Q8;
            {var subQ3=sQuery(id+"F0.wireOp",EDGE,"E48.0");Q8=makeQuery(id+"F0.imprint","IMPRINT",FACE,{"disambiguationData":[TD([[makeQuery(id+"F0.imprint","IMPRINT",EDGE,{"derivedFrom":subQ3}),-1.0]])]});}
            var Q9;
            {var subQ0=sQuery(id+"F0.wireOp",EDGE,"E35.0");Q9=makeQuery(id+"F0.imprint","IMPRINT",FACE,{"disambiguationData":[TD([[makeQuery(id+"F0.imprint","IMPRINT",EDGE,{"derivedFrom":subQ0}),-1.0]])]});}
            var Q10;
            {var subQ9=sQuery(id+"F0.wireOp",EDGE,"E51.2");var subQ10=sQuery(id+"F0.wireOp",EDGE,"E10");var subQ11=makeQuery(id+"F0.imprint","INTERSECT",VERTEX,{"derivedFrom":[subQ10,subQ9]});Q10=makeQuery(id+"F0.imprint","IMPRINT",FACE,{"disambiguationData":[TD([[makeQuery(id+"F0.imprint","IMPRINT",EDGE,{"disambiguationData":[TD([[subQ11,-1.0]])],"derivedFrom":subQ10}),-1.0]])]});}
            var Q11;
            {var subQ5=sQuery(id+"F0.wireOp",EDGE,"E51.1");Q11=makeQuery(id+"F0.imprint","IMPRINT",FACE,{"disambiguationData":[TD([[makeQuery(id+"F0.imprint","IMPRINT",EDGE,{"derivedFrom":subQ5}),-1.0]])]});}
            var Q12;
            {var subQ5=sQuery(id+"F0.wireOp",EDGE,"E51.4");Q12=makeQuery(id+"F0.imprint","IMPRINT",FACE,{"disambiguationData":[TD([[makeQuery(id+"F0.imprint","IMPRINT",EDGE,{"derivedFrom":subQ5}),-1.0]])]});}
            var Q13;
            {var subQ5=sQuery(id+"F0.wireOp",EDGE,"E50.1");Q13=makeQuery(id+"F0.imprint","IMPRINT",FACE,{"disambiguationData":[TD([[makeQuery(id+"F0.imprint","IMPRINT",EDGE,{"derivedFrom":subQ5}),-1.0]])]});}
            var Q14;
            {var subQ7=sQuery(id+"F0.wireOp",EDGE,"E52.3");var subQ11=sQuery(id+"F0.wireOp",EDGE,"E10");var subQ12=makeQuery(id+"F0.imprint","INTERSECT",VERTEX,{"derivedFrom":[subQ11,subQ7]});Q14=makeQuery(id+"F0.imprint","IMPRINT",FACE,{"disambiguationData":[TD([[makeQuery(id+"F0.imprint","IMPRINT",EDGE,{"disambiguationData":[TD([[subQ12,1.0]])],"derivedFrom":subQ11}),-1.0]])]});}
            var Q15;
            {var subQ5=sQuery(id+"F0.wireOp",EDGE,"E52.1");Q15=makeQuery(id+"F0.imprint","IMPRINT",FACE,{"disambiguationData":[TD([[makeQuery(id+"F0.imprint","IMPRINT",EDGE,{"derivedFrom":subQ5}),-1.0]])]});}
            var Q16;
            {var subQ5=sQuery(id+"F0.wireOp",EDGE,"E52.4");Q16=makeQuery(id+"F0.imprint","IMPRINT",FACE,{"disambiguationData":[TD([[makeQuery(id+"F0.imprint","IMPRINT",EDGE,{"derivedFrom":subQ5}),-1.0]])]});}
            var Q17;
            {var subQ5=sQuery(id+"F0.wireOp",EDGE,"E49.4");Q17=makeQuery(id+"F0.imprint","IMPRINT",FACE,{"disambiguationData":[TD([[makeQuery(id+"F0.imprint","IMPRINT",EDGE,{"derivedFrom":subQ5}),-1.0]])]});}
            var Q18;
            {var subQ5=sQuery(id+"F0.wireOp",EDGE,"E49.1");Q18=makeQuery(id+"F0.imprint","IMPRINT",FACE,{"disambiguationData":[TD([[makeQuery(id+"F0.imprint","IMPRINT",EDGE,{"derivedFrom":subQ5}),-1.0]])]});}
            var Q19;
            {var subQ5=sQuery(id+"F0.wireOp",EDGE,"E50.4");Q19=makeQuery(id+"F0.imprint","IMPRINT",FACE,{"disambiguationData":[TD([[makeQuery(id+"F0.imprint","IMPRINT",EDGE,{"derivedFrom":subQ5}),-1.0]])]});}
            extrude(context, id + "F2", {"entities" : qUnion([Q0, Q1, Q2, Q3, Q4, Q5, Q6, Q7, Q8, Q9, Q10, Q11, Q12, Q13, Q14, Q15, Q16, Q17, Q18, Q19]), "operationType" : NewBodyOperationType.ADD, "depth" : 0.75 * mm, "offsetDistance" : 25 * mm});
        }
        {
            var Q0;
            Q0=makeQuery(id+"F1.opExtrude","CAP_EDGE",EDGE,{"disambiguationData":[OSD([sQuery(id+"F0.wireOp",EDGE,"E56")])],"isStart":true});
            var Q1;
            Q1=makeQuery(id+"F1.opExtrude","CAP_EDGE",EDGE,{"disambiguationData":[OSD([sQuery(id+"F0.wireOp",EDGE,"E61")])],"isStart":true});
            var Q2;
            Q2=makeQuery(id+"F1.opExtrude","CAP_EDGE",EDGE,{"disambiguationData":[OSD([sQuery(id+"F0.wireOp",EDGE,"E64")])],"isStart":true});
            var Q3;
            Q3=makeQuery(id+"F1.opExtrude","CAP_EDGE",EDGE,{"disambiguationData":[OSD([sQuery(id+"F0.wireOp",EDGE,"E53")])],"isStart":true});
            var Q4;
            Q4=makeQuery(id+"F1.opExtrude","CAP_EDGE",EDGE,{"disambiguationData":[OSD([sQuery(id+"F0.wireOp",EDGE,"E63")])],"isStart":true});
            var Q5;
            Q5=makeQuery(id+"F1.opExtrude","CAP_EDGE",EDGE,{"disambiguationData":[OSD([sQuery(id+"F0.wireOp",EDGE,"E54")])],"isStart":true});
            var Q6;
            Q6=makeQuery(id+"F1.opExtrude","CAP_EDGE",EDGE,{"disambiguationData":[OSD([sQuery(id+"F0.wireOp",EDGE,"E62")])],"isStart":true});
            var Q7;
            Q7=makeQuery(id+"F1.opExtrude","CAP_EDGE",EDGE,{"disambiguationData":[OSD([sQuery(id+"F0.wireOp",EDGE,"E55")])],"isStart":true});
            var Q8;
            Q8=makeQuery(id+"F1.opExtrude","CAP_EDGE",EDGE,{"disambiguationData":[OSD([sQuery(id+"F0.wireOp",EDGE,"E55")])],"isStart":false});
            var Q9;
            Q9=makeQuery(id+"F1.opExtrude","CAP_EDGE",EDGE,{"disambiguationData":[OSD([sQuery(id+"F0.wireOp",EDGE,"E61")])],"isStart":false});
            var Q10;
            Q10=makeQuery(id+"F1.opExtrude","CAP_EDGE",EDGE,{"disambiguationData":[OSD([sQuery(id+"F0.wireOp",EDGE,"E62")])],"isStart":false});
            var Q11;
            Q11=makeQuery(id+"F1.opExtrude","CAP_EDGE",EDGE,{"disambiguationData":[OSD([sQuery(id+"F0.wireOp",EDGE,"E54")])],"isStart":false});
            var Q12;
            Q12=makeQuery(id+"F1.opExtrude","CAP_EDGE",EDGE,{"disambiguationData":[OSD([sQuery(id+"F0.wireOp",EDGE,"E63")])],"isStart":false});
            var Q13;
            Q13=makeQuery(id+"F1.opExtrude","CAP_EDGE",EDGE,{"disambiguationData":[OSD([sQuery(id+"F0.wireOp",EDGE,"E64")])],"isStart":false});
            var Q14;
            Q14=makeQuery(id+"F1.opExtrude","CAP_EDGE",EDGE,{"disambiguationData":[OSD([sQuery(id+"F0.wireOp",EDGE,"E56")])],"isStart":false});
            var Q15;
            Q15=makeQuery(id+"F1.opExtrude","CAP_EDGE",EDGE,{"disambiguationData":[OSD([sQuery(id+"F0.wireOp",EDGE,"E53")])],"isStart":false});
            fillet(context, id + "F3", {"entities" : qUnion([Q0, Q1, Q2, Q3, Q4, Q5, Q6, Q7, Q8, Q9, Q10, Q11, Q12, Q13, Q14, Q15]), "radius" : 0.75 * mm, "tangentPropagation" : true, "allowEdgeOverflow" : false});
        }
        {
            var Q0;
            Q0=makeQuery(id+"F1.opExtrude","SWEPT_EDGE",EDGE,{"disambiguationData":[OSD([sQuery(id+"F0.wireOp",EDGE,"E55"),sQuery(id+"F0.wireOp",EDGE,"E61")])]});
            var Q1;
            Q1=makeQuery(id+"F1.opExtrude","SWEPT_EDGE",EDGE,{"disambiguationData":[OSD([sQuery(id+"F0.wireOp",EDGE,"E56"),sQuery(id+"F0.wireOp",EDGE,"E64")])]});
            var Q2;
            Q2=makeQuery(id+"F1.opExtrude","SWEPT_EDGE",EDGE,{"disambiguationData":[OSD([sQuery(id+"F0.wireOp",EDGE,"E55"),sQuery(id+"F0.wireOp",EDGE,"E62")])]});
            var Q3;
            Q3=makeQuery(id+"F1.opExtrude","SWEPT_EDGE",EDGE,{"disambiguationData":[OSD([sQuery(id+"F0.wireOp",EDGE,"E54"),sQuery(id+"F0.wireOp",EDGE,"E63")])]});
            var Q4;
            Q4=makeQuery(id+"F1.opExtrude","SWEPT_EDGE",EDGE,{"disambiguationData":[OSD([sQuery(id+"F0.wireOp",EDGE,"E53"),sQuery(id+"F0.wireOp",EDGE,"E64")])]});
            var Q5;
            Q5=makeQuery(id+"F1.opExtrude","SWEPT_EDGE",EDGE,{"disambiguationData":[OSD([sQuery(id+"F0.wireOp",EDGE,"E53"),sQuery(id+"F0.wireOp",EDGE,"E63")])]});
            var Q6;
            Q6=makeQuery(id+"F1.opExtrude","SWEPT_EDGE",EDGE,{"disambiguationData":[OSD([sQuery(id+"F0.wireOp",EDGE,"E54"),sQuery(id+"F0.wireOp",EDGE,"E62")])]});
            var Q7;
            Q7=makeQuery(id+"F1.opExtrude","SWEPT_EDGE",EDGE,{"disambiguationData":[OSD([sQuery(id+"F0.wireOp",EDGE,"E56"),sQuery(id+"F0.wireOp",EDGE,"E61")])]});
            fillet(context, id + "F4", {"entities" : qUnion([Q0, Q1, Q2, Q3, Q4, Q5, Q6, Q7]), "radius" : 2 * mm, "tangentPropagation" : true, "allowEdgeOverflow" : false});
        }
    });
